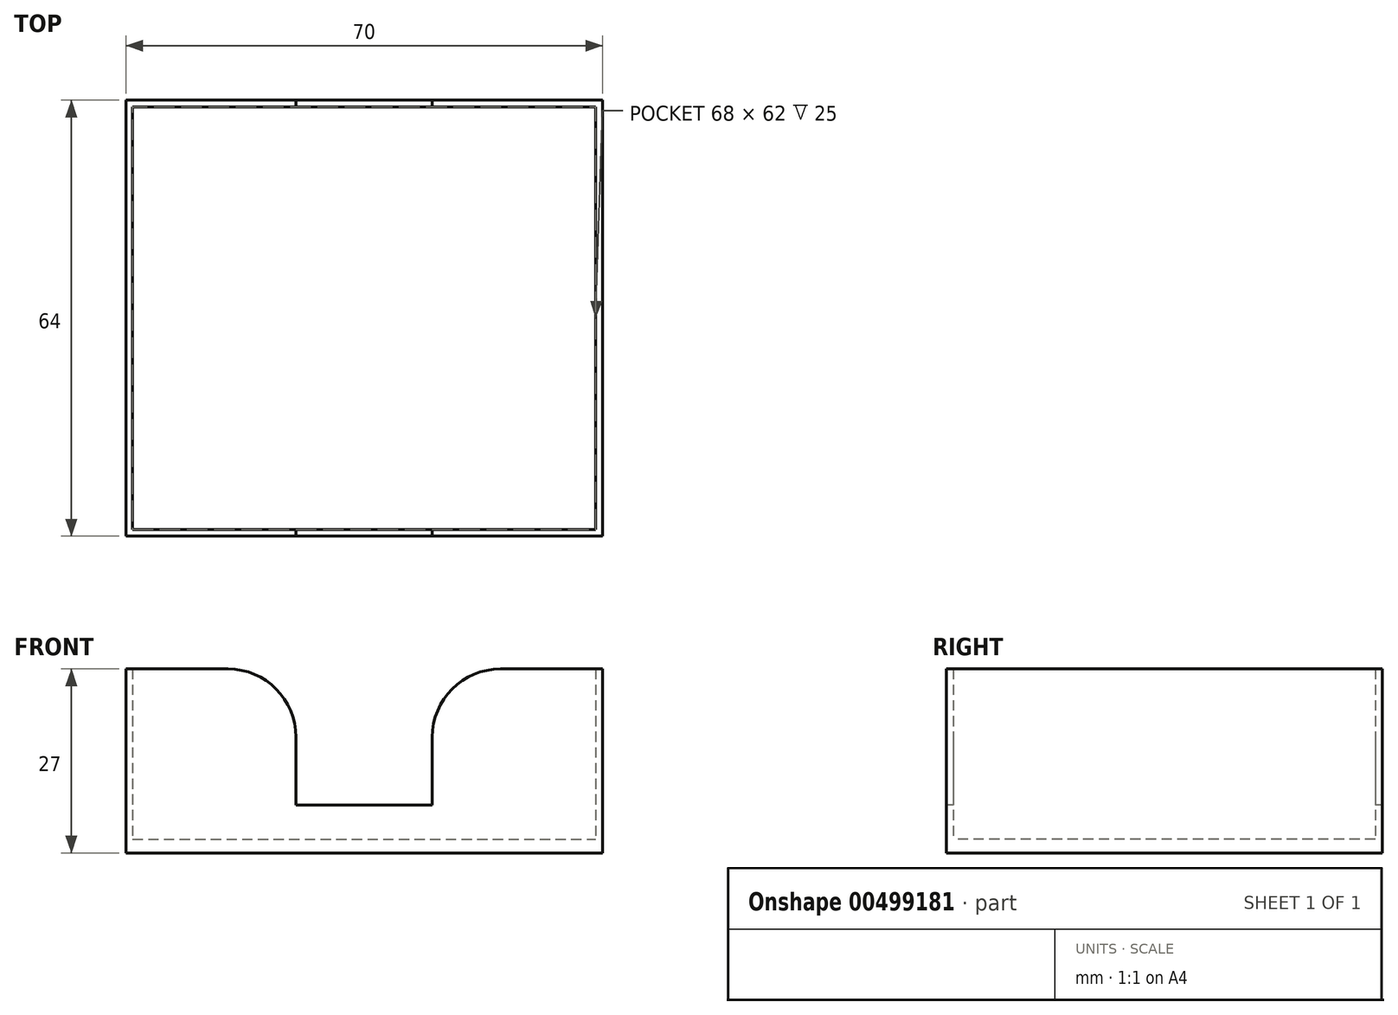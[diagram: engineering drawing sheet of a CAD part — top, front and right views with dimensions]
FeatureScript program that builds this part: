
annotation { "Feature Type Name" : "Feature", "Feature Type Description" : "" }
export const myFeature = defineFeature(function(context is Context, id is Id, definition is map)
    precondition{}
    {
        {
            var Q0;
            Q0=qCreatedBy(makeId("Top.planeOp"),FACE);
            var sketch = newSketch(context, id + "F0", { "sketchPlane" : qUnion([Q0])});
            skLineSegment(sketch, "E0.bottom", {"start": v(-35, 32) * mm, "end": v(35, 32) * mm});
            skLineSegment(sketch, "E0.top", {"start": v(-35, -32) * mm, "end": v(35, -32) * mm});
            skLineSegment(sketch, "E0.left", {"start": v(-35, 32) * mm, "end": v(-35, -32) * mm});
            skLineSegment(sketch, "E0.right", {"start": v(35, 32) * mm, "end": v(35, -32) * mm});
            skPoint(sketch, "E0.middle", {"position": v(0, 0) * mm});
            skSolve(sketch);
        }
        {
            var Q0;
            Q0=makeQuery(id+"F0.imprint","IMPRINT",FACE,{"disambiguationData":[TD([[makeQuery(id+"F0.imprint","IMPRINT",EDGE,{"derivedFrom":sQuery(id+"F0.wireOp",EDGE,"E0.bottom")}),-1.0]])]});
            extrude(context, id + "F1", {"entities" : qUnion([Q0]), "depth" : 2 * mm});
        }
        {
            var Q0;
            Q0=makeQuery(id+"F1.opExtrude","CAP_FACE",FACE,{"disambiguationData":[OSD([sQuery(id+"F0.wireOp",EDGE,"E0.bottom"),sQuery(id+"F0.wireOp",EDGE,"E0.top"),sQuery(id+"F0.wireOp",EDGE,"E0.left"),sQuery(id+"F0.wireOp",EDGE,"E0.right")])],"isStart":false});
            var sketch = newSketch(context, id + "F2", { "sketchPlane" : qUnion([Q0])});
            skLineSegment(sketch, "E1.bottom", {"start": v(-35, 32) * mm, "end": v(35, 32) * mm});
            skLineSegment(sketch, "E1.top", {"start": v(-35, -32) * mm, "end": v(35, -32) * mm});
            skLineSegment(sketch, "E1.left", {"start": v(-35, 32) * mm, "end": v(-35, -32) * mm});
            skLineSegment(sketch, "E1.right", {"start": v(35, 32) * mm, "end": v(35, -32) * mm});
            skPoint(sketch, "E1.middle", {"position": v(0, 0) * mm});
            skLineSegment(sketch, "E2.bottom", {"start": v(-34, 31) * mm, "end": v(34, 31) * mm});
            skLineSegment(sketch, "E2.top", {"start": v(-34, -31) * mm, "end": v(34, -31) * mm});
            skLineSegment(sketch, "E2.left", {"start": v(-34, 31) * mm, "end": v(-34, -31) * mm});
            skLineSegment(sketch, "E2.right", {"start": v(34, 31) * mm, "end": v(34, -31) * mm});
            skSolve(sketch);
        }
        {
            var Q0;
            Q0=makeQuery(id+"F2.imprint","IMPRINT",FACE,{"disambiguationData":[TD([[makeQuery(id+"F2.imprint","IMPRINT",EDGE,{"derivedFrom":sQuery(id+"F2.wireOp",EDGE,"E1.bottom")}),-1.0]])]});
            extrude(context, id + "F3", {"entities" : qUnion([Q0]), "operationType" : NewBodyOperationType.ADD, "depth" : 25 * mm});
        }
        {
            var Q0;
            Q0=makeQuery(id+"F3.boolean.opBoolean","MERGE",FACE,{"derivedFrom":[makeQuery(id+"F1.opExtrude","SWEPT_FACE",FACE,{"disambiguationData":[OSD([sQuery(id+"F0.wireOp",EDGE,"E0.top")])]}),makeQuery(id+"F3.opExtrude","SWEPT_FACE",FACE,{"disambiguationData":[OSD([sQuery(id+"F2.wireOp",EDGE,"E1.top")])]})]});
            var sketch = newSketch(context, id + "F4", { "sketchPlane" : qUnion([Q0])});
            skLineSegment(sketch, "E3", {"start": v(0, 27) * mm, "end": v(0, 7) * mm, "construction": true});
            skPoint(sketch, "E3.endSnap0", {"position": v(0, 27) * mm});
            skLineSegment(sketch, "E4", {"start": v(0, 7) * mm, "end": v(10, 7) * mm});
            skLineSegment(sketch, "E5", {"start": v(10, 7) * mm, "end": v(10, 17) * mm});
            skLineSegment(sketch, "E6", {"start": v(20, 27) * mm, "end": v(35, 27) * mm});
            skLineSegment(sketch, "E7", {"start": v(35, 27) * mm, "end": v(35, 0) * mm});
            skLineSegment(sketch, "E8", {"start": v(35, 0) * mm, "end": v(-35, 0) * mm});
            skLineSegment(sketch, "E9", {"start": v(-35, 0) * mm, "end": v(-35, 27) * mm});
            skLineSegment(sketch, "E10", {"start": v(0, 7) * mm, "end": v(-10, 7) * mm});
            skLineSegment(sketch, "E11", {"start": v(-10, 7) * mm, "end": v(-10, 17) * mm});
            skLineSegment(sketch, "E12", {"start": v(-20, 27) * mm, "end": v(-35, 27) * mm});
            skPoint(sketch, "E13.visualSharp", {"position": v(-10, 27) * mm});
            skArc(sketch, "E13.filletArc", {"start": v(-10, 17) * mm, "mid": v(-12.93, 24.07) * mm, "end": v(-20, 27) * mm});
            skPoint(sketch, "E14.visualSharp", {"position": v(10, 27) * mm});
            skArc(sketch, "E14.filletArc", {"start": v(20, 27) * mm, "mid": v(12.93, 24.07) * mm, "end": v(10, 17) * mm});
            skLineSegment(sketch, "E15", {"start": v(-20, 27) * mm, "end": v(20, 27) * mm});
            skSolve(sketch);
        }
        {
            var Q0;
            Q0=makeQuery(id+"F4.imprint","IMPRINT",FACE,{"disambiguationData":[TD([[makeQuery(id+"F4.imprint","IMPRINT",EDGE,{"derivedFrom":sQuery(id+"F4.wireOp",EDGE,"E4")}),1.0]])]});
            extrude(context, id + "F5", {"entities" : qUnion([Q0]), "operationType" : NewBodyOperationType.REMOVE, "oppositeDirection" : true, "depth" : 125 * mm});
        }
    });
